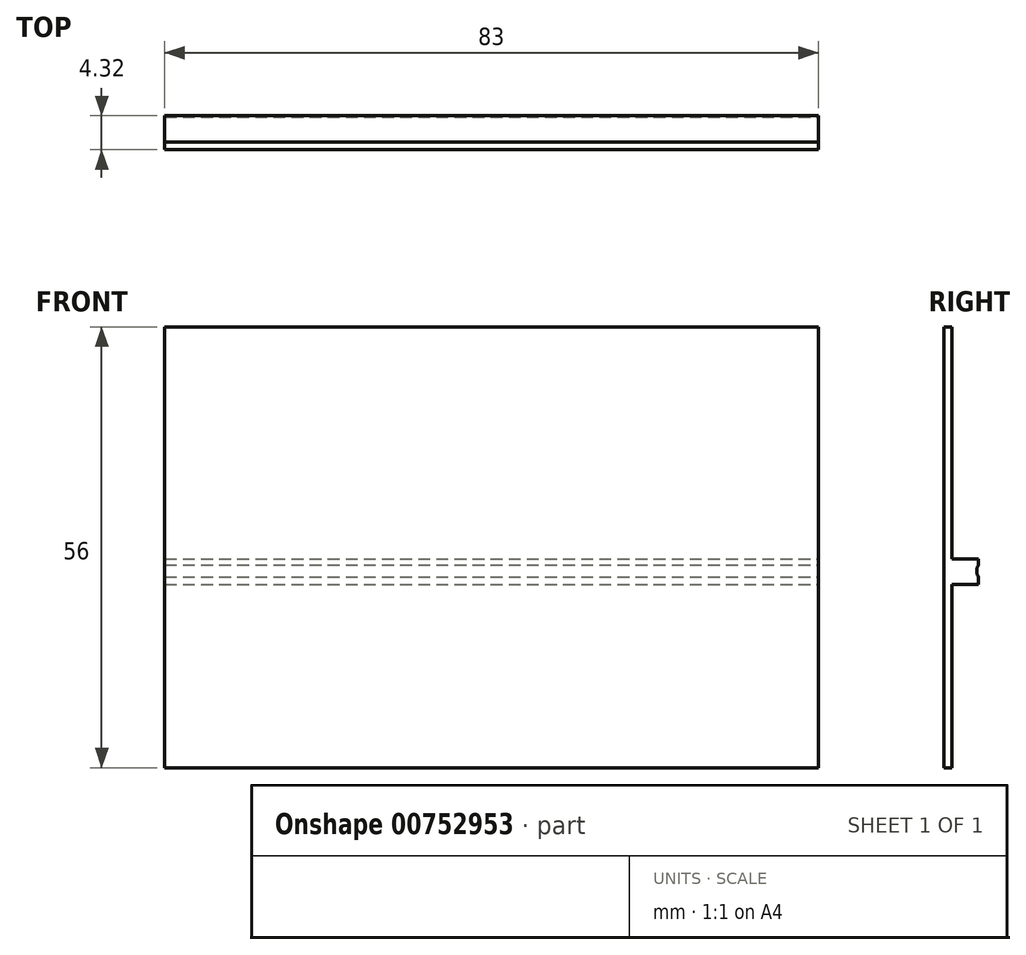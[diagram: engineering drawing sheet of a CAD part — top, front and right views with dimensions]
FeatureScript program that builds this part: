
annotation { "Feature Type Name" : "Feature", "Feature Type Description" : "" }
export const myFeature = defineFeature(function(context is Context, id is Id, definition is map)
    precondition{}
    {
        {
            var Q0;
            Q0=qCreatedBy(makeId("Front.planeOp"),FACE);
            var sketch = newSketch(context, id + "F0", { "sketchPlane" : qUnion([Q0])});
            skLineSegment(sketch, "E0.bottom", {"start": v(41.5, 28) * mm, "end": v(-41.5, 28) * mm});
            skLineSegment(sketch, "E0.top", {"start": v(41.5, -28) * mm, "end": v(-41.5, -28) * mm});
            skLineSegment(sketch, "E0.left", {"start": v(41.5, 28) * mm, "end": v(41.5, -28) * mm});
            skLineSegment(sketch, "E0.right", {"start": v(-41.5, 28) * mm, "end": v(-41.5, -28) * mm});
            skPoint(sketch, "E0.middle", {"position": v(0, 0) * mm});
            skSolve(sketch);
        }
        {
            var Q0;
            Q0=makeQuery(id+"F0.imprint","IMPRINT",FACE,{"disambiguationData":[TD([[makeQuery(id+"F0.imprint","IMPRINT",EDGE,{"derivedFrom":sQuery(id+"F0.wireOp",EDGE,"E0.bottom")}),1.0]])]});
            extrude(context, id + "F1", {"entities" : qUnion([Q0]), "depth" : 1 * mm, "offsetDistance" : 25 * mm});
        }
        {
            var Q0;
            Q0=makeQuery(id+"F1.opExtrude","SWEPT_FACE",FACE,{"disambiguationData":[OSD([sQuery(id+"F0.wireOp",EDGE,"E0.left")])]});
            var sketch = newSketch(context, id + "F2", { "sketchPlane" : qUnion([Q0])});
            skCircle(sketch, "E1", {"center": v(4.63, -3) * mm, "radius": 1.5 * mm});
            skCircle(sketch, "E2", {"center": v(1.4, 26.5) * mm, "radius": 1.5 * mm});
            skLineSegment(sketch, "E3.bottom", {"start": v(0, -1.5) * mm, "end": v(3.32, -1.5) * mm});
            skLineSegment(sketch, "E3.top", {"start": v(0, -4.73) * mm, "end": v(3.32, -4.73) * mm});
            skLineSegment(sketch, "E3.left", {"start": v(0, -1.5) * mm, "end": v(0, -4.73) * mm});
            skLineSegment(sketch, "E3.right", {"start": v(3.32, -1.5) * mm, "end": v(3.32, -4.73) * mm});
            skSolve(sketch);
        }
        {
            var Q0;
            {var subQ0=sQuery(id+"F2.wireOp",EDGE,"E1");var subQ1=makeQuery(id+"F1.opExtrude","CAP_EDGE",EDGE,{"disambiguationData":[OSD([sQuery(id+"F0.wireOp",EDGE,"E0.left")])],"isStart":true});var subQ2=makeQuery(id+"F2.imprint","INTERSECT",VERTEX,{"disambiguationData":[OD(0.0)],"derivedFrom":[subQ1,subQ0]});Q0=makeQuery(id+"F2.imprint","IMPRINT",FACE,{"disambiguationData":[TD([[makeQuery(id+"F2.imprint","IMPRINT",EDGE,{"disambiguationData":[TD([[subQ2,-1.0]])],"derivedFrom":subQ0}),1.0]])]});}
            var Q1;
            {var subQ0=sQuery(id+"F2.wireOp",EDGE,"E3.bottom");Q1=makeQuery(id+"F2.imprint","IMPRINT",FACE,{"disambiguationData":[TD([[makeQuery(id+"F2.imprint","IMPRINT",EDGE,{"derivedFrom":subQ0}),-1.0]])]});}
            var Q2;
            {var subQ0=sQuery(id+"F2.wireOp",EDGE,"E2");var subQ1=makeQuery(id+"F1.opExtrude","CAP_EDGE",EDGE,{"disambiguationData":[OSD([sQuery(id+"F0.wireOp",EDGE,"E0.left")])],"isStart":true});var subQ2=makeQuery(id+"F2.imprint","INTERSECT",VERTEX,{"disambiguationData":[OD(0.0)],"derivedFrom":[subQ1,subQ0]});Q2=makeQuery(id+"F2.imprint","IMPRINT",FACE,{"disambiguationData":[TD([[makeQuery(id+"F2.imprint","IMPRINT",EDGE,{"disambiguationData":[TD([[subQ2,-1.0]])],"derivedFrom":subQ0}),1.0]])]});}
            extrude(context, id + "F3", {"entities" : qUnion([Q0, Q1, Q2]), "operationType" : NewBodyOperationType.ADD, "oppositeDirection" : true, "depth" : 83 * mm, "offsetDistance" : 25 * mm});
        }
    });
